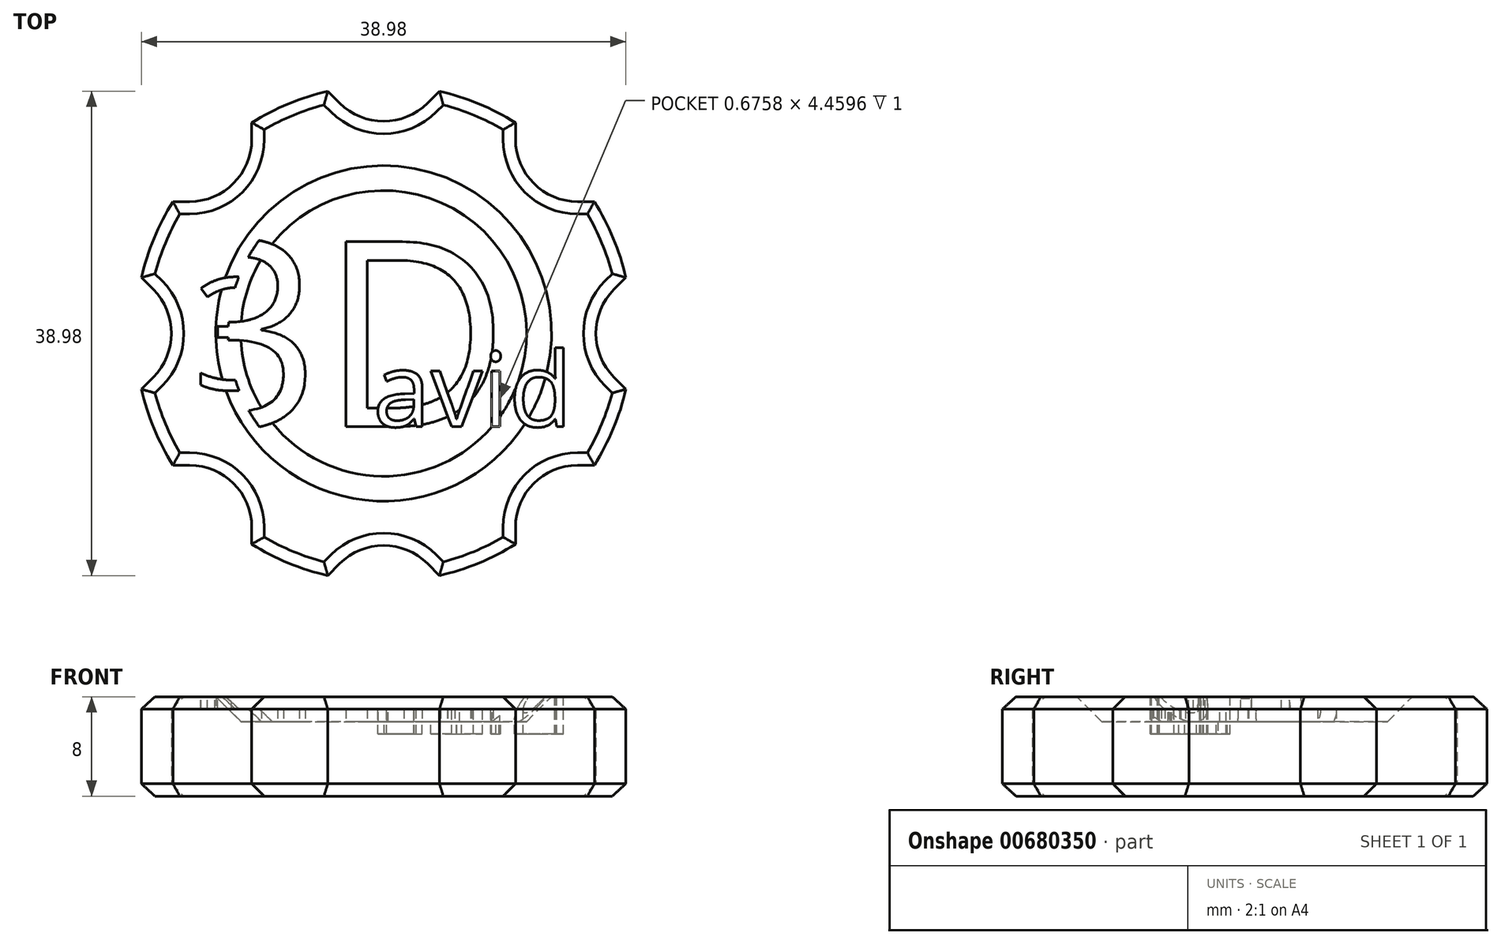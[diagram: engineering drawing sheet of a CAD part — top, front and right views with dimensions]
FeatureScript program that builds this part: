
annotation { "Feature Type Name" : "Feature", "Feature Type Description" : "" }
export const myFeature = defineFeature(function(context is Context, id is Id, definition is map)
    precondition{}
    {
        {
            var Q0;
            Q0=qCreatedBy(makeId("Top.planeOp"),FACE);
            var sketch = newSketch(context, id + "F0", { "sketchPlane" : qUnion([Q0])});
            skCircle(sketch, "E0", {"center": v(0, 0) * mm, "radius": 20 * mm});
            skLineSegment(sketch, "E1", {"start": v(-5, 20) * mm, "end": v(-3.54, 18.54) * mm});
            skLineSegment(sketch, "E2", {"start": v(3.54, 18.54) * mm, "end": v(5, 20) * mm});
            skLineSegment(sketch, "E3", {"start": v(5, 20) * mm, "end": v(-5, 20) * mm});
            skPoint(sketch, "E4.visualSharp", {"position": v(0, 15) * mm});
            skArc(sketch, "E4.filletArc", {"start": v(-3.54, 18.54) * mm, "mid": v(0, 17.07) * mm, "end": v(3.54, 18.54) * mm});
            skArc(sketch, "E5.1.0", {"start": v(-15.6, 10.6) * mm, "mid": v(-12.07, 12.07) * mm, "end": v(-10.6, 15.6) * mm});
            skLineSegment(sketch, "E5.1.1", {"start": v(-17.68, 10.6) * mm, "end": v(-15.6, 10.6) * mm});
            skLineSegment(sketch, "E5.1.2", {"start": v(-10.6, 17.68) * mm, "end": v(-17.68, 10.6) * mm});
            skLineSegment(sketch, "E5.1.3", {"start": v(-10.6, 15.6) * mm, "end": v(-10.6, 17.68) * mm});
            skArc(sketch, "E6.2.2.0", {"start": v(-18.54, -3.54) * mm, "mid": v(-17.07, 0) * mm, "end": v(-18.54, 3.54) * mm});
            skLineSegment(sketch, "E6.4.2.0", {"start": v(-20, -5) * mm, "end": v(-18.54, -3.54) * mm});
            skLineSegment(sketch, "E6.7.2.0", {"start": v(-20, 5) * mm, "end": v(-20, -5) * mm});
            skLineSegment(sketch, "E6.10.2.0", {"start": v(-18.54, 3.54) * mm, "end": v(-20, 5) * mm});
            skArc(sketch, "E6.2.3.0", {"start": v(-10.6, -15.6) * mm, "mid": v(-12.07, -12.07) * mm, "end": v(-15.6, -10.6) * mm});
            skLineSegment(sketch, "E6.4.3.0", {"start": v(-10.6, -17.68) * mm, "end": v(-10.6, -15.6) * mm});
            skLineSegment(sketch, "E6.7.3.0", {"start": v(-17.68, -10.6) * mm, "end": v(-10.6, -17.68) * mm});
            skLineSegment(sketch, "E6.10.3.0", {"start": v(-15.6, -10.6) * mm, "end": v(-17.68, -10.6) * mm});
            skArc(sketch, "E6.2.4.0", {"start": v(3.54, -18.54) * mm, "mid": v(0, -17.07) * mm, "end": v(-3.54, -18.54) * mm});
            skLineSegment(sketch, "E6.4.4.0", {"start": v(5, -20) * mm, "end": v(3.54, -18.54) * mm});
            skLineSegment(sketch, "E6.7.4.0", {"start": v(-5, -20) * mm, "end": v(5, -20) * mm});
            skLineSegment(sketch, "E6.10.4.0", {"start": v(-3.54, -18.54) * mm, "end": v(-5, -20) * mm});
            skArc(sketch, "E6.2.5.0", {"start": v(15.6, -10.6) * mm, "mid": v(12.07, -12.07) * mm, "end": v(10.6, -15.6) * mm});
            skLineSegment(sketch, "E6.4.5.0", {"start": v(17.68, -10.6) * mm, "end": v(15.6, -10.6) * mm});
            skLineSegment(sketch, "E6.7.5.0", {"start": v(10.6, -17.68) * mm, "end": v(17.68, -10.6) * mm});
            skLineSegment(sketch, "E6.10.5.0", {"start": v(10.6, -15.6) * mm, "end": v(10.6, -17.68) * mm});
            skArc(sketch, "E6.2.6.0", {"start": v(18.54, 3.54) * mm, "mid": v(17.07, 0) * mm, "end": v(18.54, -3.54) * mm});
            skLineSegment(sketch, "E6.4.6.0", {"start": v(20, 5) * mm, "end": v(18.54, 3.54) * mm});
            skLineSegment(sketch, "E6.7.6.0", {"start": v(20, -5) * mm, "end": v(20, 5) * mm});
            skLineSegment(sketch, "E6.10.6.0", {"start": v(18.54, -3.54) * mm, "end": v(20, -5) * mm});
            skArc(sketch, "E6.2.7.0", {"start": v(10.6, 15.6) * mm, "mid": v(12.07, 12.07) * mm, "end": v(15.6, 10.6) * mm});
            skLineSegment(sketch, "E6.4.7.0", {"start": v(10.6, 17.68) * mm, "end": v(10.6, 15.6) * mm});
            skLineSegment(sketch, "E6.7.7.0", {"start": v(17.68, 10.6) * mm, "end": v(10.6, 17.68) * mm});
            skLineSegment(sketch, "E6.10.7.0", {"start": v(15.6, 10.6) * mm, "end": v(17.68, 10.6) * mm});
            skCircle(sketch, "E7", {"center": v(0, 0) * mm, "radius": 12.5 * mm});
            skSolve(sketch);
        }
        {
            var Q0;
            {var subQ0=sQuery(id+"F0.wireOp",EDGE,"8eb1c374-e90a-4a47-9d3b-b4c06482910f.sketch_text.stroke-106");Q0=makeQuery(id+"F0.imprint","IMPRINT",FACE,{"disambiguationData":[TD([[makeQuery(id+"F0.imprint","IMPRINT",EDGE,{"derivedFrom":subQ0}),1.0]])]});}
            var Q1;
            {var subQ25=sQuery(id+"F0.wireOp",EDGE,"E4.filletArc");Q1=makeQuery(id+"F0.imprint","IMPRINT",FACE,{"disambiguationData":[TD([[makeQuery(id+"F0.imprint","IMPRINT",EDGE,{"derivedFrom":subQ25}),-1.0]])]});}
            extrude(context, id + "F1", {"entities" : qUnion([Q0, Q1]), "depth" : 8 * mm, "offsetDistance" : 25 * mm});
        }
        {
            var Q0;
            Q0=makeQuery(id+"F0.imprint","IMPRINT",FACE,{"disambiguationData":[TD([[makeQuery(id+"F0.imprint","IMPRINT",EDGE,{"derivedFrom":sQuery(id+"F0.wireOp",EDGE,"E7")}),1.0]])]});
            extrude(context, id + "F2", {"entities" : qUnion([Q0]), "operationType" : NewBodyOperationType.ADD, "depth" : 6 * mm, "offsetDistance" : 25 * mm});
        }
        {
            var Q0;
            Q0=makeQuery(id+"F1.opExtrude","CAP_FACE",FACE,{"disambiguationData":[OSD([sQuery(id+"F0.wireOp",EDGE,"E0"),sQuery(id+"F0.wireOp",EDGE,"E1"),sQuery(id+"F0.wireOp",EDGE,"E2"),sQuery(id+"F0.wireOp",EDGE,"E4.filletArc"),sQuery(id+"F0.wireOp",EDGE,"E5.1.0"),sQuery(id+"F0.wireOp",EDGE,"E5.1.1"),sQuery(id+"F0.wireOp",EDGE,"E5.1.3"),sQuery(id+"F0.wireOp",EDGE,"E6.2.2.0"),sQuery(id+"F0.wireOp",EDGE,"E6.4.2.0"),sQuery(id+"F0.wireOp",EDGE,"E6.10.2.0"),sQuery(id+"F0.wireOp",EDGE,"E6.2.3.0"),sQuery(id+"F0.wireOp",EDGE,"E6.4.3.0"),sQuery(id+"F0.wireOp",EDGE,"E6.10.3.0"),sQuery(id+"F0.wireOp",EDGE,"E6.2.4.0"),sQuery(id+"F0.wireOp",EDGE,"E6.4.4.0"),sQuery(id+"F0.wireOp",EDGE,"E6.10.4.0"),sQuery(id+"F0.wireOp",EDGE,"E6.2.5.0"),sQuery(id+"F0.wireOp",EDGE,"E6.4.5.0"),sQuery(id+"F0.wireOp",EDGE,"E6.10.5.0"),sQuery(id+"F0.wireOp",EDGE,"E6.2.6.0"),sQuery(id+"F0.wireOp",EDGE,"E6.4.6.0"),sQuery(id+"F0.wireOp",EDGE,"E6.10.6.0"),sQuery(id+"F0.wireOp",EDGE,"E6.2.7.0"),sQuery(id+"F0.wireOp",EDGE,"E6.4.7.0"),sQuery(id+"F0.wireOp",EDGE,"E6.10.7.0"),sQuery(id+"F0.wireOp",EDGE,"E7")])],"isStart":false});
            var Q1;
            {var subQ0=sQuery(id+"F0.wireOp",EDGE,"E7");Q1=makeQuery(id+"F2.boolean.opBoolean","MERGE",FACE,{"derivedFrom":[makeQuery(id+"F1.opExtrude","CAP_FACE",FACE,{"disambiguationData":[OSD([sQuery(id+"F0.wireOp",EDGE,"E0"),sQuery(id+"F0.wireOp",EDGE,"E1"),sQuery(id+"F0.wireOp",EDGE,"E2"),sQuery(id+"F0.wireOp",EDGE,"E4.filletArc"),sQuery(id+"F0.wireOp",EDGE,"E5.1.0"),sQuery(id+"F0.wireOp",EDGE,"E5.1.1"),sQuery(id+"F0.wireOp",EDGE,"E5.1.3"),sQuery(id+"F0.wireOp",EDGE,"E6.2.2.0"),sQuery(id+"F0.wireOp",EDGE,"E6.4.2.0"),sQuery(id+"F0.wireOp",EDGE,"E6.10.2.0"),sQuery(id+"F0.wireOp",EDGE,"E6.2.3.0"),sQuery(id+"F0.wireOp",EDGE,"E6.4.3.0"),sQuery(id+"F0.wireOp",EDGE,"E6.10.3.0"),sQuery(id+"F0.wireOp",EDGE,"E6.2.4.0"),sQuery(id+"F0.wireOp",EDGE,"E6.4.4.0"),sQuery(id+"F0.wireOp",EDGE,"E6.10.4.0"),sQuery(id+"F0.wireOp",EDGE,"E6.2.5.0"),sQuery(id+"F0.wireOp",EDGE,"E6.4.5.0"),sQuery(id+"F0.wireOp",EDGE,"E6.10.5.0"),sQuery(id+"F0.wireOp",EDGE,"E6.2.6.0"),sQuery(id+"F0.wireOp",EDGE,"E6.4.6.0"),sQuery(id+"F0.wireOp",EDGE,"E6.10.6.0"),sQuery(id+"F0.wireOp",EDGE,"E6.2.7.0"),sQuery(id+"F0.wireOp",EDGE,"E6.4.7.0"),sQuery(id+"F0.wireOp",EDGE,"E6.10.7.0"),subQ0])],"isStart":true}),makeQuery(id+"F2.opExtrude","CAP_FACE",FACE,{"disambiguationData":[OSD([subQ0])],"isStart":true})]});}
            var Q2;
            Q2=makeQuery(id+"F2.opExtrude","CAP_FACE",FACE,{"disambiguationData":[OSD([sQuery(id+"F0.wireOp",EDGE,"E7")])],"isStart":false});
            chamfer(context, id + "F3", {"entities" : qUnion([Q0, Q1, Q2]), "width" : 1 * mm, "tangentPropagation" : true});
        }
        {
            var Q0;
            Q0=makeQuery(id+"F2.opExtrude","CAP_FACE",FACE,{"disambiguationData":[OSD([sQuery(id+"F0.wireOp",EDGE,"E7")])],"isStart":false});
            var sketch = newSketch(context, id + "F4", { "sketchPlane" : qUnion([Q0])});
            skText(sketch, "E8", { "text": "3D\n", "fontName": "OpenSans-Regular.ttf"});
            const initialGuessF4  = {"E8": [-0.017, -0.0075, 1, 0, 0.015]};
            skSetInitialGuess(sketch, initialGuessF4);
            skSolve(sketch);
        }
        {
            var Q0;
            Q0 = qSketchRegion(id + "F4", true);
            extrude(context, id + "F5", {"entities" : qUnion([Q0]), "operationType" : NewBodyOperationType.ADD, "depth" : 1 * mm, "offsetDistance" : 25 * mm});
        }
        {
            var Q0;
            Q0=makeQuery(id+"F1.opExtrude","CAP_FACE",FACE,{"disambiguationData":[OSD([sQuery(id+"F0.wireOp",EDGE,"E0"),sQuery(id+"F0.wireOp",EDGE,"E1"),sQuery(id+"F0.wireOp",EDGE,"E2"),sQuery(id+"F0.wireOp",EDGE,"E4.filletArc"),sQuery(id+"F0.wireOp",EDGE,"E5.1.0"),sQuery(id+"F0.wireOp",EDGE,"E5.1.1"),sQuery(id+"F0.wireOp",EDGE,"E5.1.3"),sQuery(id+"F0.wireOp",EDGE,"E6.2.2.0"),sQuery(id+"F0.wireOp",EDGE,"E6.4.2.0"),sQuery(id+"F0.wireOp",EDGE,"E6.10.2.0"),sQuery(id+"F0.wireOp",EDGE,"E6.2.3.0"),sQuery(id+"F0.wireOp",EDGE,"E6.4.3.0"),sQuery(id+"F0.wireOp",EDGE,"E6.10.3.0"),sQuery(id+"F0.wireOp",EDGE,"E6.2.4.0"),sQuery(id+"F0.wireOp",EDGE,"E6.4.4.0"),sQuery(id+"F0.wireOp",EDGE,"E6.10.4.0"),sQuery(id+"F0.wireOp",EDGE,"E6.2.5.0"),sQuery(id+"F0.wireOp",EDGE,"E6.4.5.0"),sQuery(id+"F0.wireOp",EDGE,"E6.10.5.0"),sQuery(id+"F0.wireOp",EDGE,"E6.2.6.0"),sQuery(id+"F0.wireOp",EDGE,"E6.4.6.0"),sQuery(id+"F0.wireOp",EDGE,"E6.10.6.0"),sQuery(id+"F0.wireOp",EDGE,"E6.2.7.0"),sQuery(id+"F0.wireOp",EDGE,"E6.4.7.0"),sQuery(id+"F0.wireOp",EDGE,"E6.10.7.0"),sQuery(id+"F0.wireOp",EDGE,"E7")])],"isStart":false});
            var sketch = newSketch(context, id + "F6", { "sketchPlane" : qUnion([Q0])});
            skText(sketch, "E9", { "text": "avid\n", "fontName": "OpenSans-Regular.ttf"});
            const initialGuessF6  = {"E9": [-0.00085, -0.0075, 1, 0, 0.006]};
            skSetInitialGuess(sketch, initialGuessF6);
            skSolve(sketch);
        }
        {
            var Q0;
            Q0 = qSketchRegion(id + "F6", true);
            var Q1;
            {var subQ0=sQuery(id+"F0.wireOp",EDGE,"E7");Q1=makeQuery(id+"F5.boolean.opBoolean","SPLIT",FACE,{"disambiguationData":[TD([makeQuery(id+"F5.opExtrude","SWEPT_FACE",FACE,{"disambiguationData":[OSD([sQuery(id+"F4.wireOp",EDGE,"E8.sketch_text.stroke-0")])]})])],"derivedFrom":makeQuery(id+"F2.opExtrude","CAP_FACE",FACE,{"disambiguationData":[OSD([subQ0])],"isStart":false})});}
            extrude(context, id + "F7", {"entities" : qUnion([Q0]), "operationType" : NewBodyOperationType.REMOVE, "endBound" : BoundingType.UP_TO_SURFACE, "oppositeDirection" : true, "depth" : 4 * mm, "endBoundEntityFace" : qUnion([Q1]), "hasOffset" : true, "offsetDistance" : -1 * mm});
        }
        {
            var Q0;
            Q0=makeQuery(id+"F1.opExtrude","CAP_FACE",FACE,{"disambiguationData":[OSD([sQuery(id+"F0.wireOp",EDGE,"E0"),sQuery(id+"F0.wireOp",EDGE,"E1"),sQuery(id+"F0.wireOp",EDGE,"E2"),sQuery(id+"F0.wireOp",EDGE,"E4.filletArc"),sQuery(id+"F0.wireOp",EDGE,"E5.1.0"),sQuery(id+"F0.wireOp",EDGE,"E5.1.1"),sQuery(id+"F0.wireOp",EDGE,"E5.1.3"),sQuery(id+"F0.wireOp",EDGE,"E6.2.2.0"),sQuery(id+"F0.wireOp",EDGE,"E6.4.2.0"),sQuery(id+"F0.wireOp",EDGE,"E6.10.2.0"),sQuery(id+"F0.wireOp",EDGE,"E6.2.3.0"),sQuery(id+"F0.wireOp",EDGE,"E6.4.3.0"),sQuery(id+"F0.wireOp",EDGE,"E6.10.3.0"),sQuery(id+"F0.wireOp",EDGE,"E6.2.4.0"),sQuery(id+"F0.wireOp",EDGE,"E6.4.4.0"),sQuery(id+"F0.wireOp",EDGE,"E6.10.4.0"),sQuery(id+"F0.wireOp",EDGE,"E6.2.5.0"),sQuery(id+"F0.wireOp",EDGE,"E6.4.5.0"),sQuery(id+"F0.wireOp",EDGE,"E6.10.5.0"),sQuery(id+"F0.wireOp",EDGE,"E6.2.6.0"),sQuery(id+"F0.wireOp",EDGE,"E6.4.6.0"),sQuery(id+"F0.wireOp",EDGE,"E6.10.6.0"),sQuery(id+"F0.wireOp",EDGE,"E6.2.7.0"),sQuery(id+"F0.wireOp",EDGE,"E6.4.7.0"),sQuery(id+"F0.wireOp",EDGE,"E6.10.7.0"),sQuery(id+"F0.wireOp",EDGE,"E7")])],"isStart":false});
            var sketch = newSketch(context, id + "F8", { "sketchPlane" : qUnion([Q0])});
            skText(sketch, "E10", { "text": "3D\n", "fontName": "OpenSans-Regular.ttf"});
            const initialGuessF8  = {"E10": [-0.0153, -0.0045, 1, 0, 0.009]};
            skSetInitialGuess(sketch, initialGuessF8);
            skSolve(sketch);
        }
        {
            var Q0;
            Q0 = qSketchRegion(id + "F8", true);
            var Q1;
            Q1=makeQuery(id+"F5.opExtrude","CAP_FACE",FACE,{"disambiguationData":[OSD([sQuery(id+"F4.wireOp",EDGE,"E8.sketch_text.stroke-28"),sQuery(id+"F4.wireOp",EDGE,"E8.sketch_text.stroke-29"),sQuery(id+"F4.wireOp",EDGE,"E8.sketch_text.stroke-30"),sQuery(id+"F4.wireOp",EDGE,"E8.sketch_text.stroke-31"),sQuery(id+"F4.wireOp",EDGE,"E8.sketch_text.stroke-32"),sQuery(id+"F4.wireOp",EDGE,"E8.sketch_text.stroke-33"),sQuery(id+"F4.wireOp",EDGE,"E8.sketch_text.stroke-34"),sQuery(id+"F4.wireOp",EDGE,"E8.sketch_text.stroke-35"),sQuery(id+"F4.wireOp",EDGE,"E8.sketch_text.stroke-36"),sQuery(id+"F4.wireOp",EDGE,"E8.sketch_text.stroke-37"),sQuery(id+"F4.wireOp",EDGE,"E8.sketch_text.stroke-38"),sQuery(id+"F4.wireOp",EDGE,"E8.sketch_text.stroke-39"),sQuery(id+"F4.wireOp",EDGE,"E8.sketch_text.stroke-40"),sQuery(id+"F4.wireOp",EDGE,"E8.sketch_text.stroke-41")])],"isStart":false});
            extrude(context, id + "F9", {"entities" : qUnion([Q0]), "operationType" : NewBodyOperationType.REMOVE, "endBound" : BoundingType.UP_TO_SURFACE, "oppositeDirection" : true, "depth" : 1 * mm, "endBoundEntityFace" : qUnion([Q1]), "offsetDistance" : 25 * mm});
        }
    });
